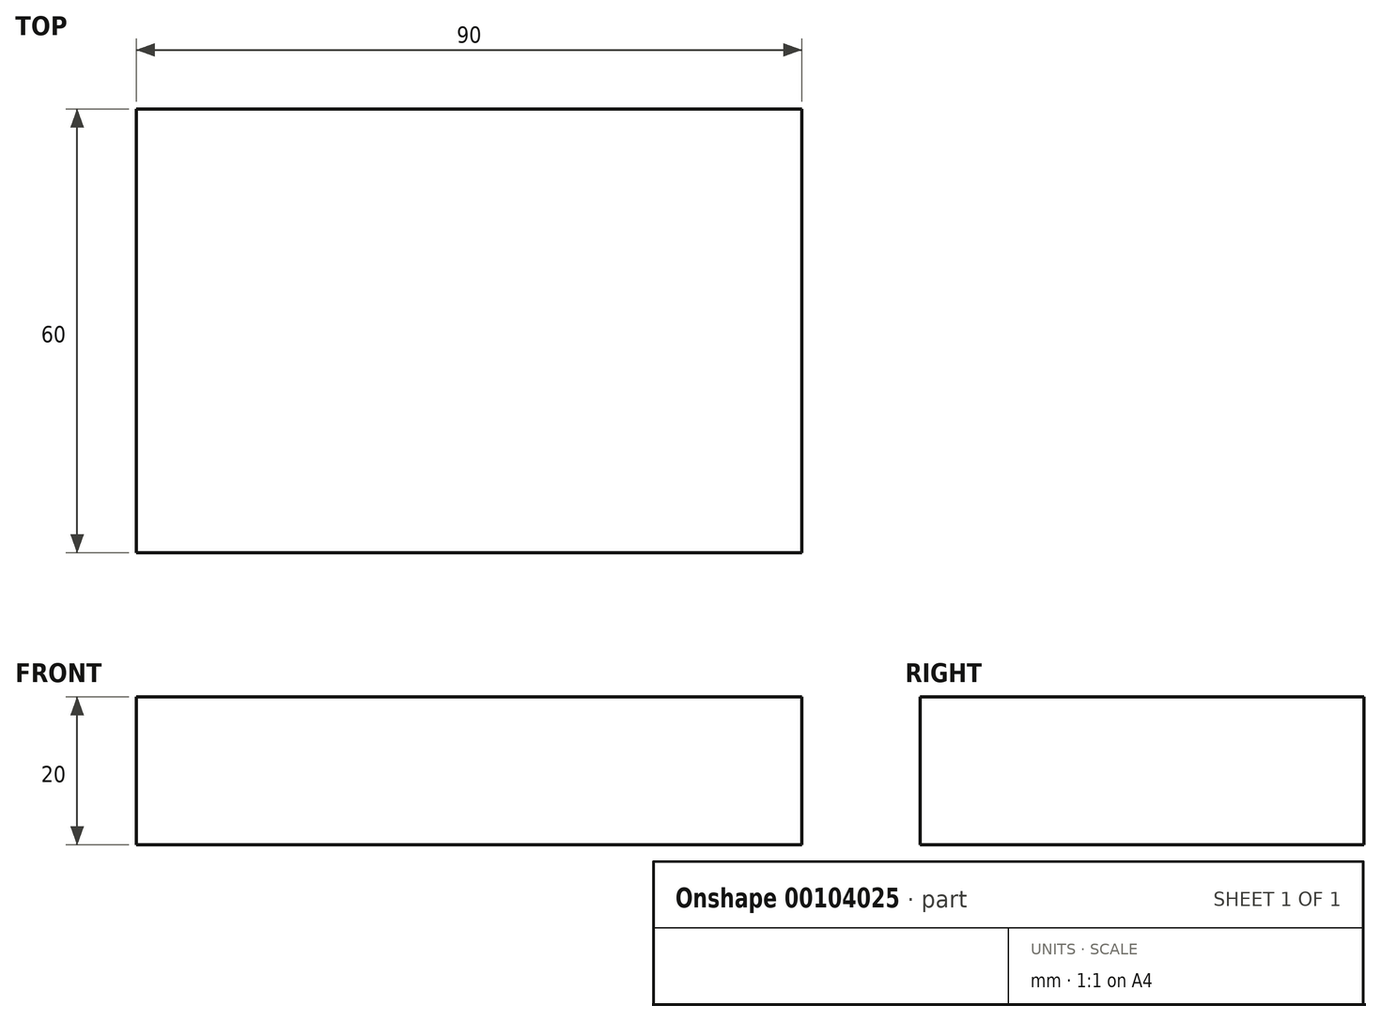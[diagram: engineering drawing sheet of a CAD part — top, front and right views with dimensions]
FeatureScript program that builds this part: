
annotation { "Feature Type Name" : "Feature", "Feature Type Description" : "" }
export const myFeature = defineFeature(function(context is Context, id is Id, definition is map)
    precondition{}
    {
        {
            var Q0;
            Q0=qCreatedBy(makeId("Top.planeOp"),FACE);
            var sketch = newSketch(context, id + "F0", { "sketchPlane" : qUnion([Q0])});
            skLineSegment(sketch, "E0.bottom", {"start": v(-47.73, 39.51) * mm, "end": v(42.27, 39.51) * mm});
            skLineSegment(sketch, "E0.top", {"start": v(-47.73, -20.49) * mm, "end": v(42.27, -20.49) * mm});
            skLineSegment(sketch, "E0.left", {"start": v(-47.73, 39.51) * mm, "end": v(-47.73, -20.49) * mm});
            skLineSegment(sketch, "E0.right", {"start": v(42.27, 39.51) * mm, "end": v(42.27, -20.49) * mm});
            skSolve(sketch);
        }
        {
            var Q0;
            Q0 = qSketchRegion(id + "F0", true);
            extrude(context, id + "F1", {"entities" : qUnion([Q0]), "depth" : 20 * mm, "offsetDistance" : 25 * mm});
        }
    });
